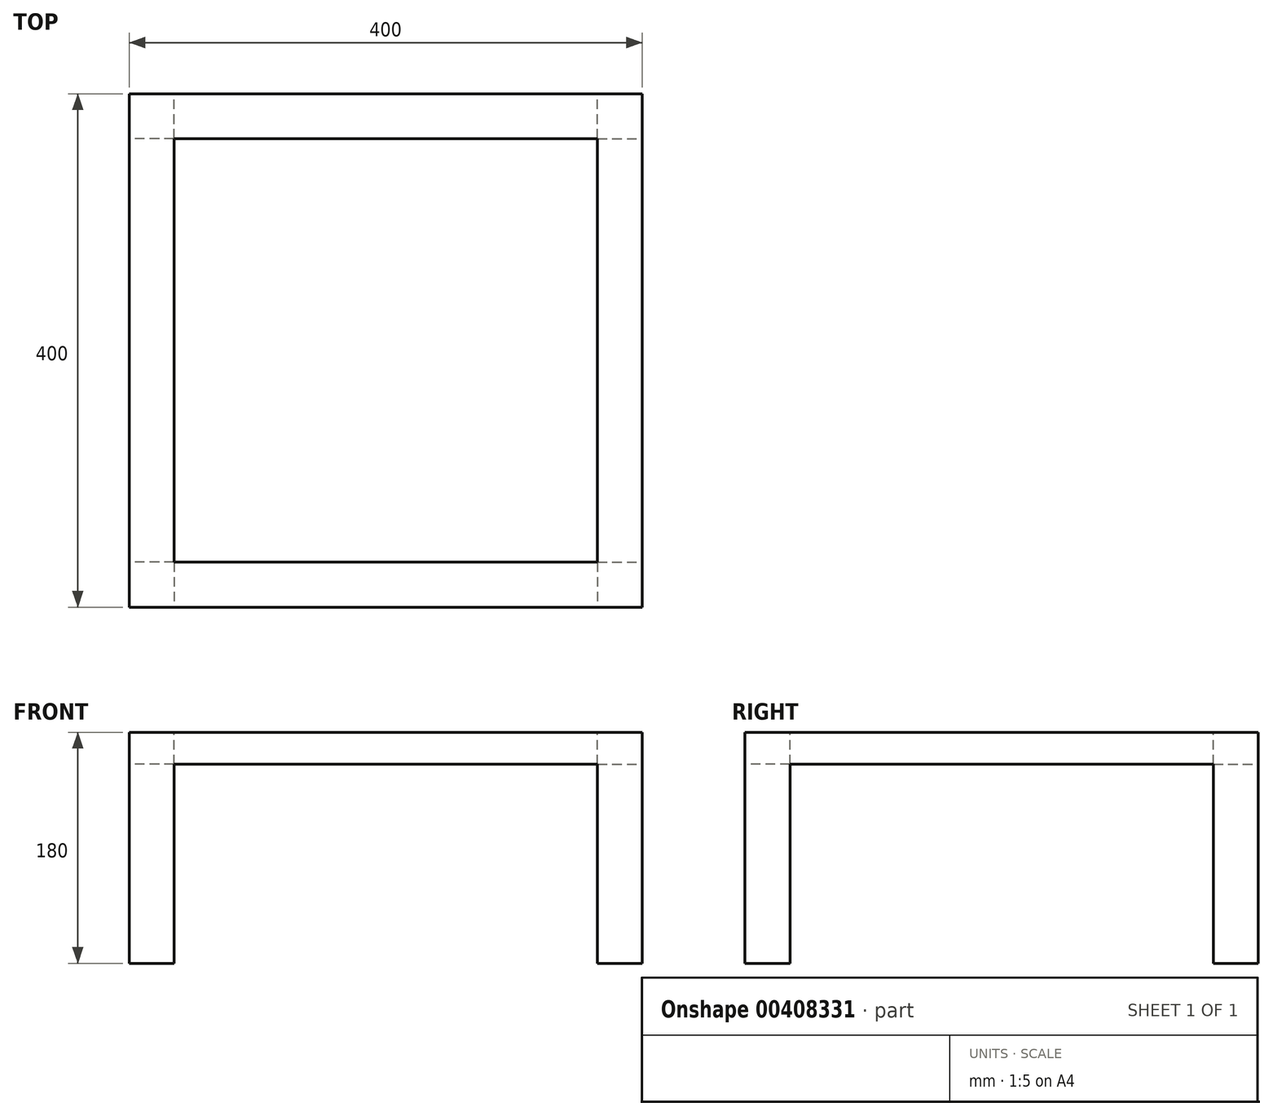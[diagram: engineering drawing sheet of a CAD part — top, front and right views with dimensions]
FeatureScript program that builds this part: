
annotation { "Feature Type Name" : "Feature", "Feature Type Description" : "" }
export const myFeature = defineFeature(function(context is Context, id is Id, definition is map)
    precondition{}
    {
        {
            var Q0;
            Q0=qCreatedBy(makeId("Top.planeOp"),FACE);
            var sketch = newSketch(context, id + "F0", { "sketchPlane" : qUnion([Q0])});
            skLineSegment(sketch, "E0.bottom", {"start": v(200, 200) * mm, "end": v(-200, 200) * mm});
            skLineSegment(sketch, "E0.top", {"start": v(200, -200) * mm, "end": v(-200, -200) * mm});
            skLineSegment(sketch, "E0.left", {"start": v(200, 200) * mm, "end": v(200, -200) * mm});
            skLineSegment(sketch, "E0.right", {"start": v(-200, 200) * mm, "end": v(-200, -200) * mm});
            skPoint(sketch, "E0.middle", {"position": v(0, 0) * mm});
            skLineSegment(sketch, "E1.bottom", {"start": v(165, 165) * mm, "end": v(-165, 165) * mm});
            skLineSegment(sketch, "E1.top", {"start": v(165, -165) * mm, "end": v(-165, -165) * mm});
            skLineSegment(sketch, "E1.left", {"start": v(165, 165) * mm, "end": v(165, -165) * mm});
            skLineSegment(sketch, "E1.right", {"start": v(-165, 165) * mm, "end": v(-165, -165) * mm});
            skSolve(sketch);
        }
        {
            var Q0;
            Q0=makeQuery(id+"F0.imprint","IMPRINT",FACE,{"disambiguationData":[TD([[makeQuery(id+"F0.imprint","IMPRINT",EDGE,{"derivedFrom":sQuery(id+"F0.wireOp",EDGE,"E0.bottom")}),1.0]])]});
            extrude(context, id + "F1", {"entities" : qUnion([Q0]), "oppositeDirection" : true, "depth" : 25 * mm});
        }
        {
            var Q0;
            Q0=makeQuery(id+"F1.opExtrude","CAP_FACE",FACE,{"disambiguationData":[OSD([sQuery(id+"F0.wireOp",EDGE,"E0.bottom"),sQuery(id+"F0.wireOp",EDGE,"E0.top"),sQuery(id+"F0.wireOp",EDGE,"E0.left"),sQuery(id+"F0.wireOp",EDGE,"E0.right"),sQuery(id+"F0.wireOp",EDGE,"E1.bottom"),sQuery(id+"F0.wireOp",EDGE,"E1.top"),sQuery(id+"F0.wireOp",EDGE,"E1.left"),sQuery(id+"F0.wireOp",EDGE,"E1.right")])],"isStart":false});
            var sketch = newSketch(context, id + "F2", { "sketchPlane" : qUnion([Q0])});
            skLineSegment(sketch, "E2.bottom", {"start": v(-165, 165) * mm, "end": v(-200, 165) * mm});
            skLineSegment(sketch, "E2.top", {"start": v(-165, 200) * mm, "end": v(-200, 200) * mm});
            skLineSegment(sketch, "E2.left", {"start": v(-165, 165) * mm, "end": v(-165, 200) * mm});
            skLineSegment(sketch, "E2.right", {"start": v(-200, 165) * mm, "end": v(-200, 200) * mm});
            skLineSegment(sketch, "E3.bottom", {"start": v(165, 165) * mm, "end": v(200, 165) * mm});
            skLineSegment(sketch, "E3.top", {"start": v(165, 200) * mm, "end": v(200, 200) * mm});
            skLineSegment(sketch, "E3.left", {"start": v(165, 165) * mm, "end": v(165, 200) * mm});
            skLineSegment(sketch, "E3.right", {"start": v(200, 165) * mm, "end": v(200, 200) * mm});
            skLineSegment(sketch, "E4.bottom", {"start": v(165, -165) * mm, "end": v(200, -165) * mm});
            skLineSegment(sketch, "E4.top", {"start": v(165, -200) * mm, "end": v(200, -200) * mm});
            skLineSegment(sketch, "E4.left", {"start": v(165, -165) * mm, "end": v(165, -200) * mm});
            skLineSegment(sketch, "E4.right", {"start": v(200, -165) * mm, "end": v(200, -200) * mm});
            skLineSegment(sketch, "E5.bottom", {"start": v(-165, -165) * mm, "end": v(-200, -165) * mm});
            skLineSegment(sketch, "E5.top", {"start": v(-165, -200) * mm, "end": v(-200, -200) * mm});
            skLineSegment(sketch, "E5.left", {"start": v(-165, -165) * mm, "end": v(-165, -200) * mm});
            skLineSegment(sketch, "E5.right", {"start": v(-200, -165) * mm, "end": v(-200, -200) * mm});
            skSolve(sketch);
        }
        {
            var Q0;
            Q0=makeQuery(id+"F2.imprint","IMPRINT",FACE,{"disambiguationData":[TD([[makeQuery(id+"F2.imprint","IMPRINT",EDGE,{"derivedFrom":sQuery(id+"F2.wireOp",EDGE,"E2.bottom")}),-1.0]])]});
            var Q1;
            Q1=makeQuery(id+"F2.imprint","IMPRINT",FACE,{"disambiguationData":[TD([[makeQuery(id+"F2.imprint","IMPRINT",EDGE,{"derivedFrom":sQuery(id+"F2.wireOp",EDGE,"E3.bottom")}),1.0]])]});
            var Q2;
            Q2=makeQuery(id+"F2.imprint","IMPRINT",FACE,{"disambiguationData":[TD([[makeQuery(id+"F2.imprint","IMPRINT",EDGE,{"derivedFrom":sQuery(id+"F2.wireOp",EDGE,"E4.bottom")}),-1.0]])]});
            var Q3;
            Q3=makeQuery(id+"F2.imprint","IMPRINT",FACE,{"disambiguationData":[TD([[makeQuery(id+"F2.imprint","IMPRINT",EDGE,{"derivedFrom":sQuery(id+"F2.wireOp",EDGE,"E5.bottom")}),1.0]])]});
            extrude(context, id + "F3", {"entities" : qUnion([Q0, Q1, Q2, Q3]), "operationType" : NewBodyOperationType.ADD, "depth" : (180 - 25) * mm});
        }
    });
